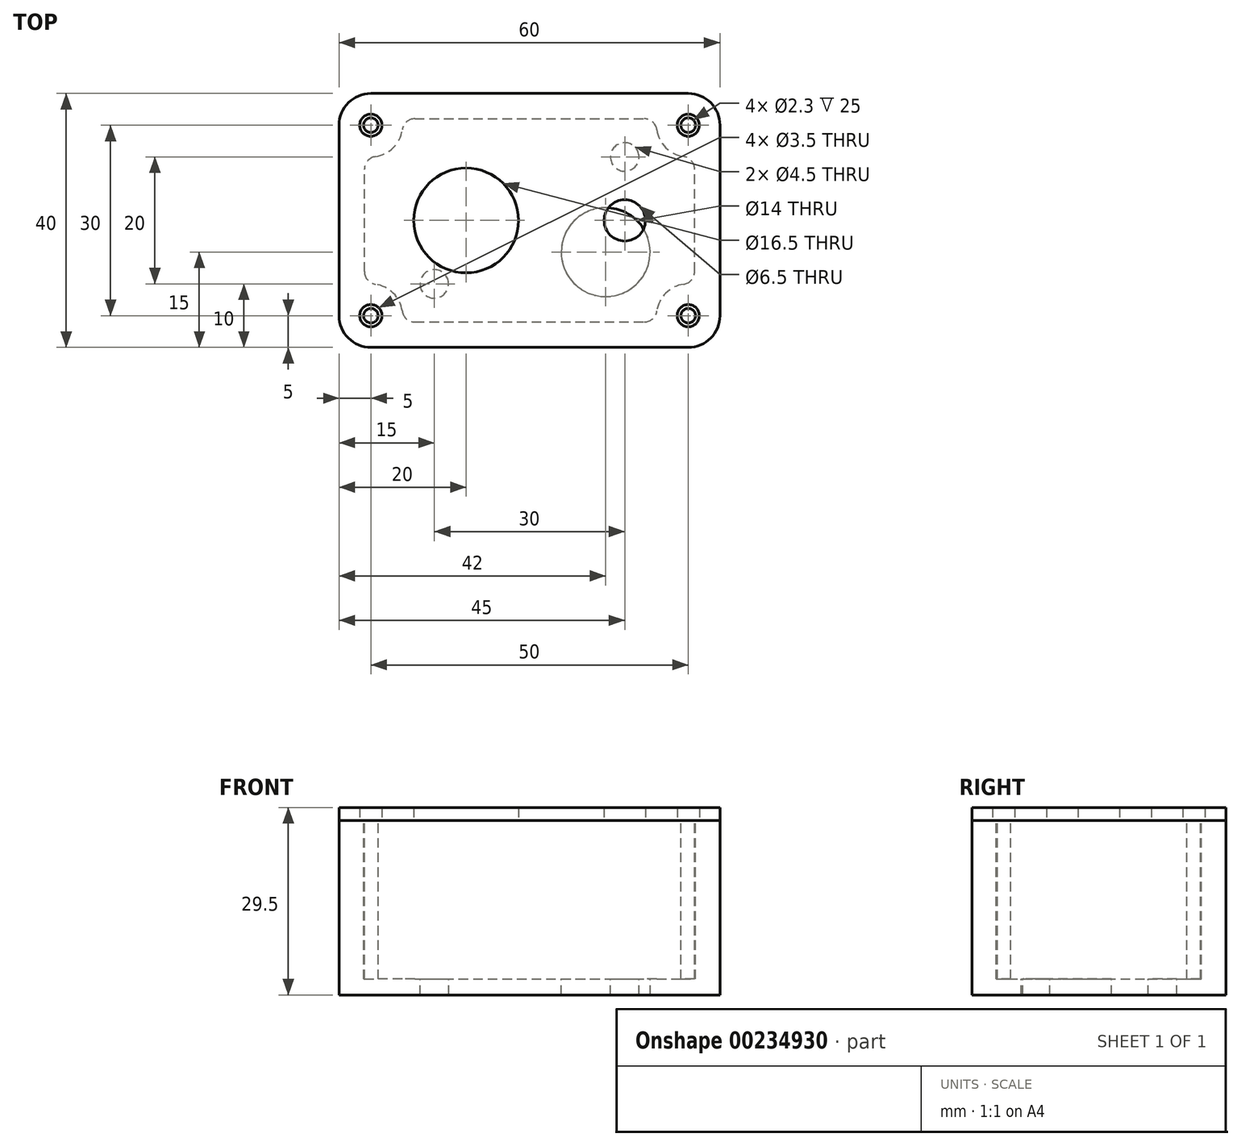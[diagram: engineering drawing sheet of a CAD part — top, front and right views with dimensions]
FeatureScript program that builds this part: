
annotation { "Feature Type Name" : "Feature", "Feature Type Description" : "" }
export const myFeature = defineFeature(function(context is Context, id is Id, definition is map)
    precondition{}
    {
        {
            var Q0;
            Q0=qCreatedBy(makeId("Top.planeOp"),FACE);
            var sketch = newSketch(context, id + "F0", { "sketchPlane" : qUnion([Q0])});
            skLineSegment(sketch, "E0.bottom", {"start": v(5, 0) * mm, "end": v(55, 0) * mm});
            skLineSegment(sketch, "E0.top", {"start": v(5, 40) * mm, "end": v(55, 40) * mm});
            skLineSegment(sketch, "E0.left", {"start": v(0, 5) * mm, "end": v(0, 35) * mm});
            skLineSegment(sketch, "E0.right", {"start": v(60, 5) * mm, "end": v(60, 35) * mm});
            skLineSegment(sketch, "E1", {"start": v(0, 20) * mm, "end": v(60, 20) * mm, "construction": true});
            skCircle(sketch, "E2", {"center": v(20, 20) * mm, "radius": 8.25 * mm});
            skCircle(sketch, "E3", {"center": v(45, 20) * mm, "radius": 3.25 * mm});
            skPoint(sketch, "E4.visualSharp", {"position": v(60, 40) * mm});
            skArc(sketch, "E4.filletArc", {"start": v(60, 35) * mm, "mid": v(58.54, 38.54) * mm, "end": v(55, 40) * mm});
            skPoint(sketch, "E5.visualSharp", {"position": v(60, 0) * mm});
            skArc(sketch, "E5.filletArc", {"start": v(55, 0) * mm, "mid": v(58.54, 1.46) * mm, "end": v(60, 5) * mm});
            skPoint(sketch, "E6.visualSharp", {"position": v(0, 0) * mm});
            skArc(sketch, "E6.filletArc", {"start": v(0, 5) * mm, "mid": v(1.46, 1.46) * mm, "end": v(5, 0) * mm});
            skPoint(sketch, "E7.visualSharp", {"position": v(0, 40) * mm});
            skArc(sketch, "E7.filletArc", {"start": v(5, 40) * mm, "mid": v(1.46, 38.54) * mm, "end": v(0, 35) * mm});
            skCircle(sketch, "E8", {"center": v(55, 35) * mm, "radius": 1.75 * mm});
            skCircle(sketch, "E9", {"center": v(5, 35) * mm, "radius": 1.75 * mm});
            skCircle(sketch, "E10.MirrorC", {"center": v(5, 5) * mm, "radius": 1.75 * mm});
            skCircle(sketch, "E11.MirrorC", {"center": v(55, 5) * mm, "radius": 1.75 * mm});
            skSolve(sketch);
        }
        {
            var Q0;
            Q0 = qSketchRegion(id + "F0", true);
            extrude(context, id + "F1", {"entities" : qUnion([Q0]), "depth" : 2 * mm});
        }
        {
            var Q0;
            Q0=makeQuery(id+"F1.opExtrude","CAP_FACE",FACE,{"disambiguationData":[OSD([sQuery(id+"F0.wireOp",EDGE,"E0.bottom"),sQuery(id+"F0.wireOp",EDGE,"E0.top"),sQuery(id+"F0.wireOp",EDGE,"E0.left"),sQuery(id+"F0.wireOp",EDGE,"E0.right"),sQuery(id+"F0.wireOp",EDGE,"E2"),sQuery(id+"F0.wireOp",EDGE,"E3"),sQuery(id+"F0.wireOp",EDGE,"E4.filletArc"),sQuery(id+"F0.wireOp",EDGE,"E5.filletArc"),sQuery(id+"F0.wireOp",EDGE,"E6.filletArc"),sQuery(id+"F0.wireOp",EDGE,"E7.filletArc"),sQuery(id+"F0.wireOp",EDGE,"E8"),sQuery(id+"F0.wireOp",EDGE,"E9"),sQuery(id+"F0.wireOp",EDGE,"E10.MirrorC"),sQuery(id+"F0.wireOp",EDGE,"E11.MirrorC")])],"isStart":true});
            var sketch = newSketch(context, id + "F2", { "sketchPlane" : qUnion([Q0])});
            skCircle(sketch, "E12.0", {"center": v(55, -5) * mm, "radius": 1.75 * mm, "construction": true});
            skLineSegment(sketch, "E13.0", {"start": v(5, 0) * mm, "end": v(55, 0) * mm});
            skArc(sketch, "E14.0", {"start": v(55, 0) * mm, "mid": v(58.54, -1.46) * mm, "end": v(60, -5) * mm});
            skLineSegment(sketch, "E15.0", {"start": v(60, -5) * mm, "end": v(60, -35) * mm});
            skPoint(sketch, "E16.0", {"position": v(58.54, -38.54) * mm});
            skLineSegment(sketch, "E17.0", {"start": v(5, -40) * mm, "end": v(55, -40) * mm});
            skCircle(sketch, "E18.0", {"center": v(5, -35) * mm, "radius": 1.75 * mm, "construction": true});
            skCircle(sketch, "E19.0", {"center": v(5, -5) * mm, "radius": 1.75 * mm, "construction": true});
            skCircle(sketch, "E20.0", {"center": v(55, -35) * mm, "radius": 1.75 * mm, "construction": true});
            skArc(sketch, "E21.0", {"start": v(0, -5) * mm, "mid": v(1.46, -1.46) * mm, "end": v(5, 0) * mm});
            skLineSegment(sketch, "E22.0", {"start": v(0, -5) * mm, "end": v(0, -35) * mm});
            skArc(sketch, "E23.0", {"start": v(5, -40) * mm, "mid": v(1.46, -38.54) * mm, "end": v(0, -35) * mm});
            skArc(sketch, "E24.0", {"start": v(60, -35) * mm, "mid": v(58.54, -38.54) * mm, "end": v(55, -40) * mm});
            skArc(sketch, "E25.0", {"start": v(5.71, -9.95) * mm, "mid": v(8.54, -8.54) * mm, "end": v(9.95, -5.71) * mm});
            skLineSegment(sketch, "E26.0", {"start": v(11.93, -4) * mm, "end": v(48.07, -4) * mm});
            skLineSegment(sketch, "E27.0", {"start": v(56, -11.93) * mm, "end": v(56, -28.07) * mm});
            skLineSegment(sketch, "E28.0", {"start": v(11.93, -36) * mm, "end": v(48.07, -36) * mm});
            skLineSegment(sketch, "E29.0", {"start": v(4, -11.93) * mm, "end": v(4, -28.07) * mm});
            skPoint(sketch, "E30.visualSharp", {"position": v(4, -9.9) * mm});
            skArc(sketch, "E30.filletArc", {"start": v(5.71, -9.95) * mm, "mid": v(4.49, -10.62) * mm, "end": v(4, -11.93) * mm});
            skPoint(sketch, "E31.visualSharp", {"position": v(9.9, -4) * mm});
            skArc(sketch, "E31.filletArc", {"start": v(11.93, -4) * mm, "mid": v(10.62, -4.49) * mm, "end": v(9.95, -5.71) * mm});
            skLineSegment(sketch, "E32", {"start": v(30, 0) * mm, "end": v(30, -40) * mm, "construction": true});
            skLineSegment(sketch, "E33", {"start": v(0, -20) * mm, "end": v(60, -20) * mm, "construction": true});
            skArc(sketch, "E34.MirrorCS", {"start": v(54.29, -9.95) * mm, "mid": v(55.51, -10.62) * mm, "end": v(56, -11.93) * mm});
            skArc(sketch, "E35.MirrorCS", {"start": v(54.29, -9.95) * mm, "mid": v(51.46, -8.54) * mm, "end": v(50.05, -5.71) * mm});
            skArc(sketch, "E36.MirrorCS", {"start": v(48.07, -4) * mm, "mid": v(49.38, -4.49) * mm, "end": v(50.05, -5.71) * mm});
            skArc(sketch, "E37.MirrorCS", {"start": v(5.71, -30.05) * mm, "mid": v(4.49, -29.38) * mm, "end": v(4, -28.07) * mm});
            skArc(sketch, "E38.MirrorCS", {"start": v(5.71, -30.05) * mm, "mid": v(8.54, -31.46) * mm, "end": v(9.95, -34.29) * mm});
            skArc(sketch, "E39.MirrorCS", {"start": v(11.93, -36) * mm, "mid": v(10.62, -35.51) * mm, "end": v(9.95, -34.29) * mm});
            skArc(sketch, "E40.MirrorCS", {"start": v(48.07, -36) * mm, "mid": v(49.38, -35.51) * mm, "end": v(50.05, -34.29) * mm});
            skArc(sketch, "E41.MirrorCS", {"start": v(54.29, -30.05) * mm, "mid": v(51.46, -31.46) * mm, "end": v(50.05, -34.29) * mm});
            skArc(sketch, "E42.MirrorCS", {"start": v(54.29, -30.05) * mm, "mid": v(55.51, -29.38) * mm, "end": v(56, -28.07) * mm});
            skCircle(sketch, "E43", {"center": v(5, -5) * mm, "radius": 1.15 * mm});
            skCircle(sketch, "E44", {"center": v(55, -5) * mm, "radius": 1.15 * mm});
            skCircle(sketch, "E45", {"center": v(55, -35) * mm, "radius": 1.15 * mm});
            skCircle(sketch, "E46", {"center": v(5, -35) * mm, "radius": 1.15 * mm});
            skSolve(sketch);
        }
        {
            var Q0;
            Q0 = qSketchRegion(id + "F2", true);
            extrude(context, id + "F3", {"entities" : qUnion([Q0]), "depth" : 25 * mm});
        }
        {
            var Q0;
            Q0=makeQuery(id+"F3.opExtrude","CAP_FACE",FACE,{"disambiguationData":[OSD([sQuery(id+"F2.wireOp",EDGE,"E13.0"),sQuery(id+"F2.wireOp",EDGE,"E14.0"),sQuery(id+"F2.wireOp",EDGE,"E15.0"),sQuery(id+"F2.wireOp",EDGE,"E17.0"),sQuery(id+"F2.wireOp",EDGE,"E21.0"),sQuery(id+"F2.wireOp",EDGE,"E22.0"),sQuery(id+"F2.wireOp",EDGE,"E23.0"),sQuery(id+"F2.wireOp",EDGE,"E24.0"),sQuery(id+"F2.wireOp",EDGE,"E25.0"),sQuery(id+"F2.wireOp",EDGE,"E26.0"),sQuery(id+"F2.wireOp",EDGE,"E27.0"),sQuery(id+"F2.wireOp",EDGE,"E28.0"),sQuery(id+"F2.wireOp",EDGE,"E29.0"),sQuery(id+"F2.wireOp",EDGE,"E30.filletArc"),sQuery(id+"F2.wireOp",EDGE,"E31.filletArc"),sQuery(id+"F2.wireOp",EDGE,"E34.MirrorCS"),sQuery(id+"F2.wireOp",EDGE,"E35.MirrorCS"),sQuery(id+"F2.wireOp",EDGE,"E36.MirrorCS"),sQuery(id+"F2.wireOp",EDGE,"E37.MirrorCS"),sQuery(id+"F2.wireOp",EDGE,"E38.MirrorCS"),sQuery(id+"F2.wireOp",EDGE,"E39.MirrorCS"),sQuery(id+"F2.wireOp",EDGE,"E40.MirrorCS"),sQuery(id+"F2.wireOp",EDGE,"E41.MirrorCS"),sQuery(id+"F2.wireOp",EDGE,"E42.MirrorCS"),sQuery(id+"F2.wireOp",EDGE,"E43"),sQuery(id+"F2.wireOp",EDGE,"E44"),sQuery(id+"F2.wireOp",EDGE,"E45"),sQuery(id+"F2.wireOp",EDGE,"E46")])],"isStart":false});
            var sketch = newSketch(context, id + "F4", { "sketchPlane" : qUnion([Q0])});
            skLineSegment(sketch, "E47.0", {"start": v(5, 0) * mm, "end": v(55, 0) * mm});
            skArc(sketch, "E48.0", {"start": v(0, -5) * mm, "mid": v(1.46, -1.46) * mm, "end": v(5, 0) * mm});
            skLineSegment(sketch, "E48.1", {"start": v(0, -5) * mm, "end": v(0, -35) * mm});
            skArc(sketch, "E49.0", {"start": v(5, -40) * mm, "mid": v(1.46, -38.54) * mm, "end": v(0, -35) * mm});
            skLineSegment(sketch, "E49.1", {"start": v(5, -40) * mm, "end": v(55, -40) * mm});
            skLineSegment(sketch, "E49.2", {"start": v(60, -5) * mm, "end": v(60, -35) * mm});
            skArc(sketch, "E49.3", {"start": v(55, 0) * mm, "mid": v(58.54, -1.46) * mm, "end": v(60, -5) * mm});
            skPoint(sketch, "E49.4", {"position": v(58.54, -38.54) * mm});
            skArc(sketch, "E50.0", {"start": v(60, -35) * mm, "mid": v(58.54, -38.54) * mm, "end": v(55, -40) * mm});
            skCircle(sketch, "E51", {"center": v(42, -15) * mm, "radius": 7 * mm});
            skLineSegment(sketch, "E52", {"start": v(30, 0) * mm, "end": v(30, -40) * mm});
            skCircle(sketch, "E53", {"center": v(15, -10) * mm, "radius": 6 * mm, "construction": true});
            skCircle(sketch, "E54", {"center": v(15, -10) * mm, "radius": 2.25 * mm});
            skCircle(sketch, "E55", {"center": v(45, -30) * mm, "radius": 2.25 * mm});
            skCircle(sketch, "E56", {"center": v(45, -30) * mm, "radius": 6 * mm, "construction": true});
            skSolve(sketch);
        }
        {
            var Q0;
            Q0 = qSketchRegion(id + "F4", true);
            extrude(context, id + "F5", {"entities" : qUnion([Q0]), "operationType" : NewBodyOperationType.ADD, "depth" : 2.5 * mm});
        }
    });
